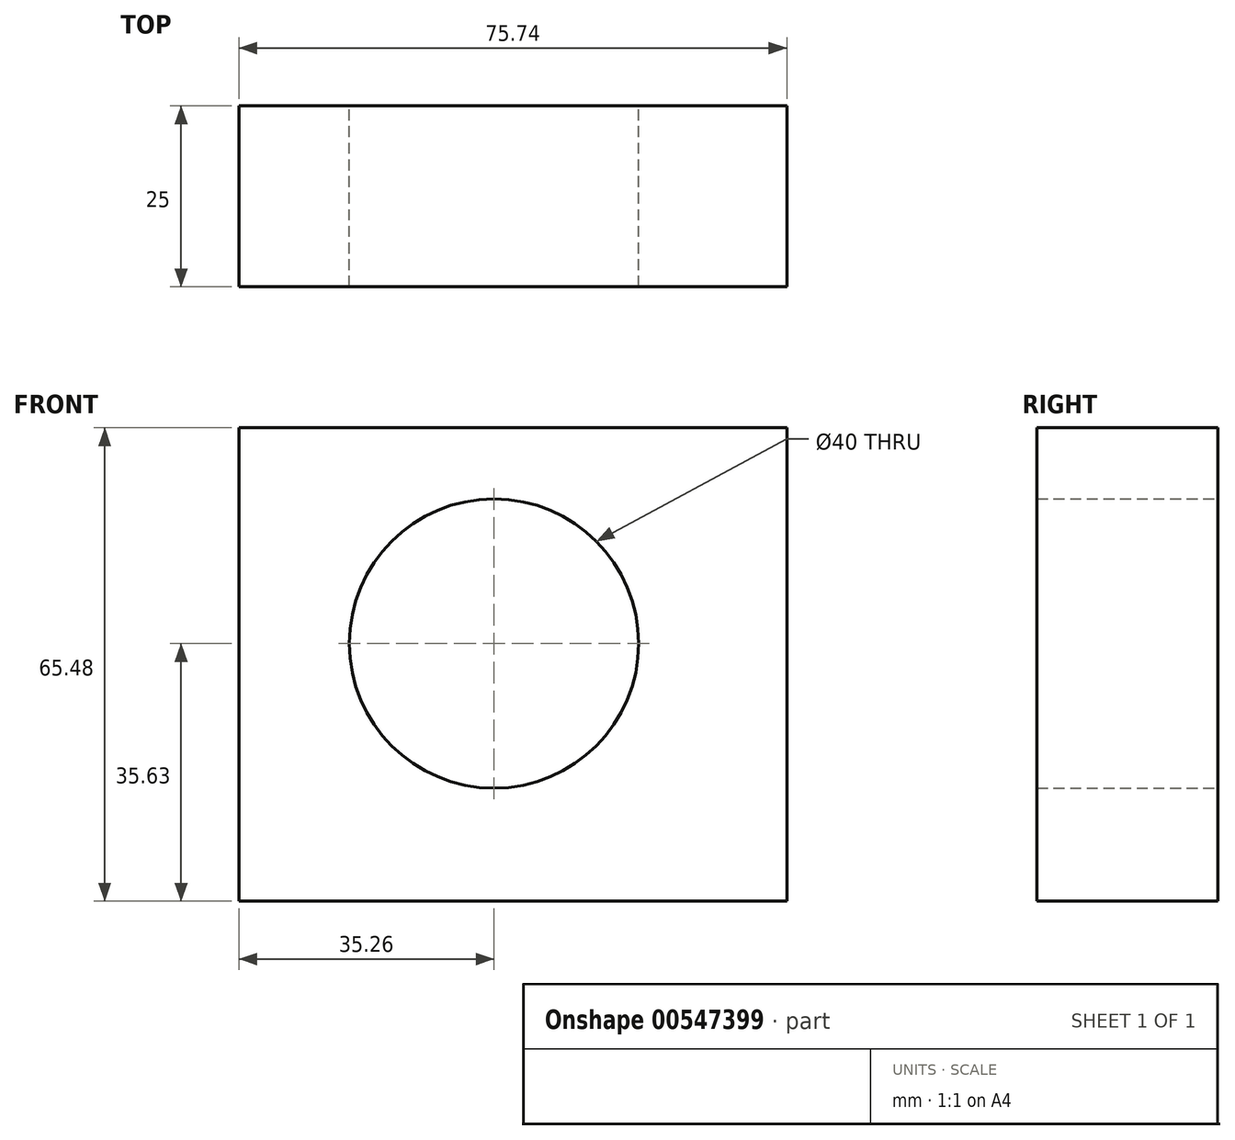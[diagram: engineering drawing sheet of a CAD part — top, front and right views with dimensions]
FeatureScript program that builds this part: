
annotation { "Feature Type Name" : "Feature", "Feature Type Description" : "" }
export const myFeature = defineFeature(function(context is Context, id is Id, definition is map)
    precondition{}
    {
        {
            var Q0;
            Q0=qCreatedBy(makeId("Front.planeOp"),FACE);
            var sketch = newSketch(context, id + "F0", { "sketchPlane" : qUnion([Q0])});
            skCircle(sketch, "E0", {"center": v(0, 0) * mm, "radius": 20 * mm});
            skLineSegment(sketch, "E1.bottom", {"start": v(-35.26, 29.85) * mm, "end": v(40.48, 29.85) * mm});
            skLineSegment(sketch, "E1.top", {"start": v(-35.26, -35.63) * mm, "end": v(40.48, -35.63) * mm});
            skLineSegment(sketch, "E1.left", {"start": v(-35.26, 29.85) * mm, "end": v(-35.26, -35.63) * mm});
            skLineSegment(sketch, "E1.right", {"start": v(40.48, 29.85) * mm, "end": v(40.48, -35.63) * mm});
            skSolve(sketch);
        }
        {
            var Q0;
            Q0=makeQuery(id+"F0.imprint","IMPRINT",FACE,{"disambiguationData":[TD([[makeQuery(id+"F0.imprint","IMPRINT",EDGE,{"derivedFrom":sQuery(id+"F0.wireOp",EDGE,"E0")}),-1.0]])]});
            extrude(context, id + "F1", {"entities" : qUnion([Q0]), "depth" : 25 * mm, "offsetDistance" : 25 * mm});
        }
    });
